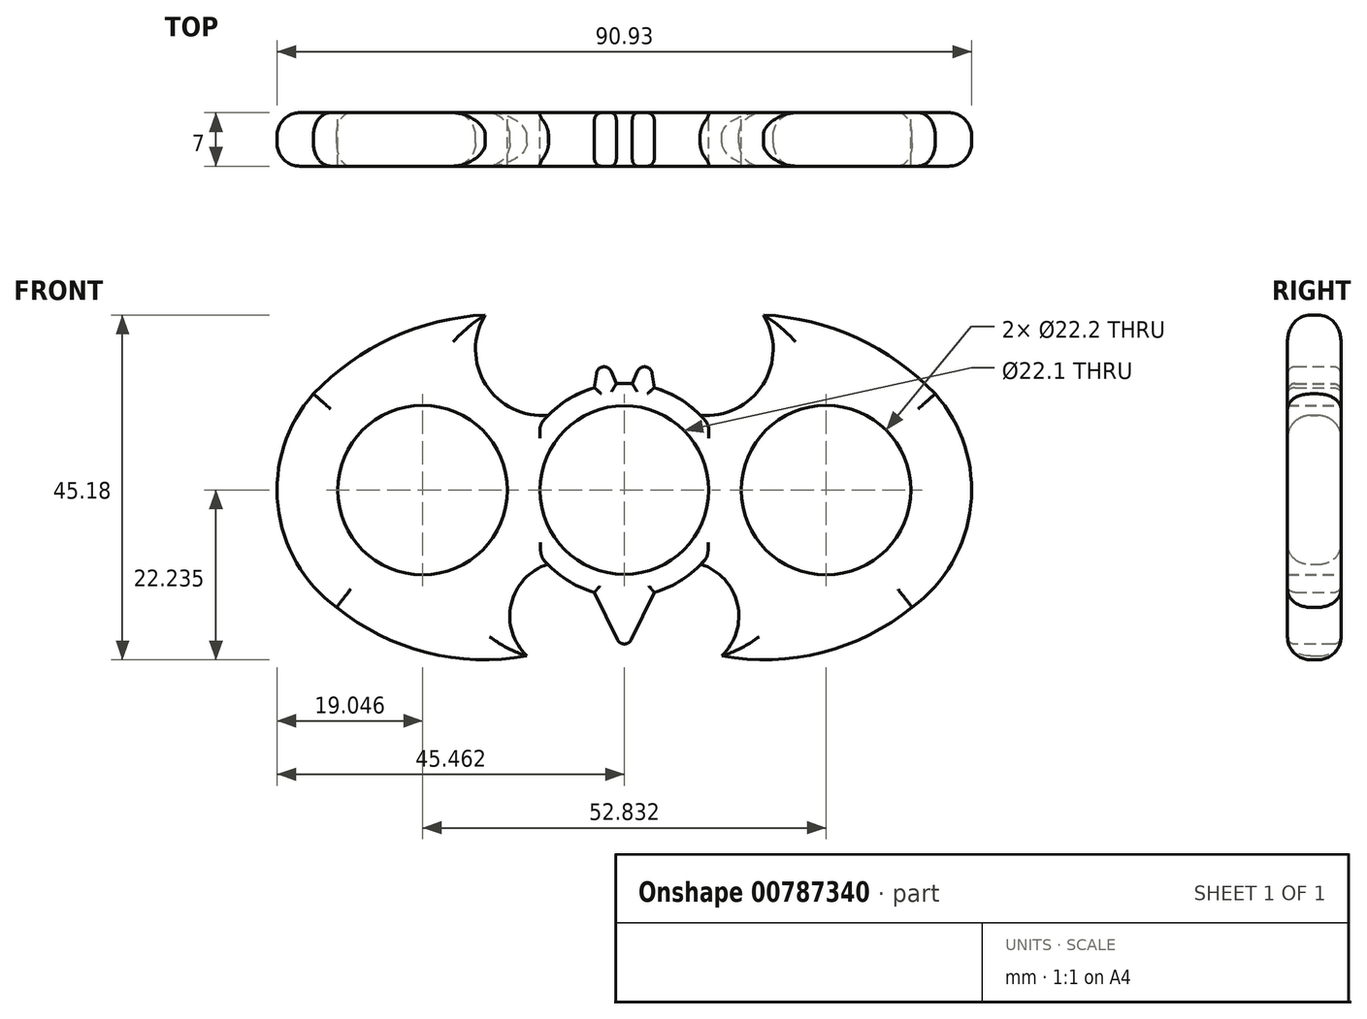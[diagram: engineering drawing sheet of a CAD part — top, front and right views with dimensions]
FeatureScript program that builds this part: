
annotation { "Feature Type Name" : "Feature", "Feature Type Description" : "" }
export const myFeature = defineFeature(function(context is Context, id is Id, definition is map)
    precondition{}
    {
        {
            var Q0;
            Q0=qCreatedBy(makeId("Front.planeOp"),FACE);
            var sketch = newSketch(context, id + "F0", { "sketchPlane" : qUnion([Q0])});
            skCircle(sketch, "E0", {"center": v(17.42, -21.9) * mm, "radius": 11.05 * mm});
            skCircle(sketch, "E1", {"center": v(17.42, -21.9) * mm, "radius": 13.97 * mm});
            skArc(sketch, "E2", {"start": v(55.1, -37.26) * mm, "mid": v(62.78, -23.94) * mm, "end": v(58.12, -9.3) * mm});
            skArc(sketch, "E3", {"start": v(-0.79, 1.05) * mm, "mid": v(-13.03, -1.96) * mm, "end": v(-23.28, -9.3) * mm});
            skArc(sketch, "E4", {"start": v(-0.79, 1.05) * mm, "mid": v(-0.73, -8.08) * mm, "end": v(7.5, -12.07) * mm});
            skArc(sketch, "E5.trimOffspring", {"start": v(-23.28, -9.3) * mm, "mid": v(-27.93, -23.94) * mm, "end": v(-20.26, -37.26) * mm});
            skArc(sketch, "E6.MirrorCS", {"start": v(35.63, 1.05) * mm, "mid": v(35.57, -8.08) * mm, "end": v(27.35, -12.07) * mm});
            skArc(sketch, "E7.MirrorCS", {"start": v(35.63, 1.05) * mm, "mid": v(47.87, -1.96) * mm, "end": v(58.12, -9.3) * mm});
            skArc(sketch, "E8", {"start": v(-20.26, -37.26) * mm, "mid": v(-8.5, -43.17) * mm, "end": v(4.66, -43.63) * mm});
            skArc(sketch, "E9", {"start": v(7.39, -31.62) * mm, "mid": v(2.6, -36.85) * mm, "end": v(4.66, -43.63) * mm});
            skArc(sketch, "E10.MirrorCS", {"start": v(27.45, -31.62) * mm, "mid": v(32.23, -36.85) * mm, "end": v(30.18, -43.63) * mm});
            skArc(sketch, "E11.MirrorCS", {"start": v(55.1, -37.26) * mm, "mid": v(43.34, -43.17) * mm, "end": v(30.18, -43.63) * mm});
            skPoint(sketch, "E12.end.orphan", {"position": v(19.76, -3.07) * mm});
            skPoint(sketch, "E13.orphan", {"position": v(21.34, -8.49) * mm});
            skPoint(sketch, "E14.end.orphan", {"position": v(16.38, -7.96) * mm});
            skPoint(sketch, "E15.end.orphan", {"position": v(15.2, -3.07) * mm});
            skPoint(sketch, "E16.MirrorCS.end.orphan", {"position": v(18.46, -7.96) * mm});
            skPoint(sketch, "E16.MirrorCS.start.orphan", {"position": v(19.65, -3.07) * mm});
            skPoint(sketch, "E17.end.orphan", {"position": v(12.61, -3.54) * mm});
            skPoint(sketch, "E18.MirrorCS.end.orphan", {"position": v(22.23, -3.54) * mm});
            skLineSegment(sketch, "E19", {"start": v(16.38, -7.96) * mm, "end": v(14.32, -3.06) * mm});
            skLineSegment(sketch, "E20", {"start": v(14.32, -3.06) * mm, "end": v(13.5, -8.49) * mm});
            skLineSegment(sketch, "E21.MirrorCS", {"start": v(18.46, -7.96) * mm, "end": v(20.52, -3.06) * mm});
            skLineSegment(sketch, "E22.MirrorCS", {"start": v(20.52, -3.06) * mm, "end": v(21.34, -8.49) * mm});
            skPoint(sketch, "E23.end.orphan", {"position": v(17.42, -43.35) * mm});
            skPoint(sketch, "E23.start.orphan", {"position": v(13.41, -35.28) * mm});
            skPoint(sketch, "E24.MirrorCS.start.orphan", {"position": v(21.43, -35.28) * mm});
            skPoint(sketch, "E25.MirrorCS.end.orphan", {"position": v(13.5, -35.3) * mm});
            skPoint(sketch, "E25.MirrorCS.start.orphan", {"position": v(14.32, -40.73) * mm});
            skLineSegment(sketch, "E26", {"start": v(13.5, -35.3) * mm, "end": v(17.42, -43.35) * mm});
            skLineSegment(sketch, "E27.MirrorCS", {"start": v(21.34, -35.3) * mm, "end": v(17.42, -43.35) * mm});
            skLineSegment(sketch, "E28", {"start": v(-9, -21.9) * mm, "end": v(-13.74, -21.9) * mm});
            skLineSegment(sketch, "E29", {"start": v(43.84, -21.9) * mm, "end": v(48.58, -21.9) * mm});
            skCircle(sketch, "E30", {"center": v(-9, -21.9) * mm, "radius": 11.1 * mm});
            skCircle(sketch, "E31", {"center": v(43.84, -21.9) * mm, "radius": 11.1 * mm});
            skSolve(sketch);
        }
        {
            var Q0;
            Q0=makeQuery(id+"F0.imprint","IMPRINT",FACE,{"disambiguationData":[TD([[makeQuery(id+"F0.imprint","IMPRINT",EDGE,{"derivedFrom":sQuery(id+"F0.wireOp",EDGE,"E3")}),1.0]])]});
            var Q1;
            {var subQ0=sQuery(id+"F0.wireOp",EDGE,"E21.MirrorCS");Q1=makeQuery(id+"F0.imprint","IMPRINT",FACE,{"disambiguationData":[TD([[makeQuery(id+"F0.imprint","IMPRINT",EDGE,{"derivedFrom":subQ0}),-1.0]])]});}
            var Q2;
            {var subQ0=sQuery(id+"F0.wireOp",EDGE,"E19");Q2=makeQuery(id+"F0.imprint","IMPRINT",FACE,{"disambiguationData":[TD([[makeQuery(id+"F0.imprint","IMPRINT",EDGE,{"derivedFrom":subQ0}),1.0]])]});}
            var Q3;
            {var subQ0=sQuery(id+"F0.wireOp",EDGE,"E26");Q3=makeQuery(id+"F0.imprint","IMPRINT",FACE,{"disambiguationData":[TD([[makeQuery(id+"F0.imprint","IMPRINT",EDGE,{"derivedFrom":subQ0}),1.0]])]});}
            var Q4;
            Q4=makeQuery(id+"F0.imprint","IMPRINT",FACE,{"disambiguationData":[TD([[makeQuery(id+"F0.imprint","IMPRINT",EDGE,{"derivedFrom":sQuery(id+"F0.wireOp",EDGE,"E0")}),-1.0]])]});
            var Q5;
            Q5=makeQuery(id+"F0.imprint","IMPRINT",FACE,{"disambiguationData":[TD([[makeQuery(id+"F0.imprint","IMPRINT",EDGE,{"derivedFrom":sQuery(id+"F0.wireOp",EDGE,"E2")}),1.0]])]});
            extrude(context, id + "F1", {"entities" : qUnion([Q0, Q1, Q2, Q3, Q4, Q5]), "depth" : 7 * mm, "offsetDistance" : 25 * mm});
        }
        {
            var Q0;
            Q0=makeQuery(id+"F1.opExtrude","CAP_EDGE",EDGE,{"disambiguationData":[OSD([sQuery(id+"F0.wireOp",EDGE,"E5.trimOffspring")])],"isStart":false});
            var Q1;
            Q1=makeQuery(id+"F1.opExtrude","CAP_EDGE",EDGE,{"disambiguationData":[OSD([sQuery(id+"F0.wireOp",EDGE,"E2")])],"isStart":false});
            var Q2;
            Q2=makeQuery(id+"F1.opExtrude","CAP_EDGE",EDGE,{"disambiguationData":[OSD([sQuery(id+"F0.wireOp",EDGE,"E3")])],"isStart":true});
            var Q3;
            Q3=makeQuery(id+"F1.opExtrude","CAP_EDGE",EDGE,{"disambiguationData":[OSD([sQuery(id+"F0.wireOp",EDGE,"E7.MirrorCS")])],"isStart":true});
            var Q4;
            Q4=makeQuery(id+"F1.opExtrude","CAP_EDGE",EDGE,{"disambiguationData":[OSD([sQuery(id+"F0.wireOp",EDGE,"E6.MirrorCS")])],"isStart":false});
            var Q5;
            Q5=makeQuery(id+"F1.opExtrude","CAP_EDGE",EDGE,{"disambiguationData":[OSD([sQuery(id+"F0.wireOp",EDGE,"E10.MirrorCS")])],"isStart":false});
            var Q6;
            Q6=makeQuery(id+"F1.opExtrude","CAP_EDGE",EDGE,{"disambiguationData":[OSD([sQuery(id+"F0.wireOp",EDGE,"E9")])],"isStart":false});
            var Q7;
            Q7=makeQuery(id+"F1.opExtrude","CAP_EDGE",EDGE,{"disambiguationData":[OSD([sQuery(id+"F0.wireOp",EDGE,"E4")])],"isStart":false});
            var Q8;
            Q8=makeQuery(id+"F1.opExtrude","CAP_EDGE",EDGE,{"disambiguationData":[OSD([sQuery(id+"F0.wireOp",EDGE,"E4")])],"isStart":true});
            var Q9;
            Q9=makeQuery(id+"F1.opExtrude","CAP_EDGE",EDGE,{"disambiguationData":[OSD([sQuery(id+"F0.wireOp",EDGE,"E9")])],"isStart":true});
            var Q10;
            Q10=makeQuery(id+"F1.opExtrude","CAP_EDGE",EDGE,{"disambiguationData":[OSD([sQuery(id+"F0.wireOp",EDGE,"E6.MirrorCS")])],"isStart":true});
            var Q11;
            Q11=makeQuery(id+"F1.opExtrude","CAP_EDGE",EDGE,{"disambiguationData":[OSD([sQuery(id+"F0.wireOp",EDGE,"E10.MirrorCS")])],"isStart":true});
            var Q12;
            Q12=makeQuery(id+"F1.opExtrude","CAP_EDGE",EDGE,{"disambiguationData":[OSD([sQuery(id+"F0.wireOp",EDGE,"E11.MirrorCS")])],"isStart":true});
            var Q13;
            Q13=makeQuery(id+"F1.opExtrude","CAP_EDGE",EDGE,{"disambiguationData":[OSD([sQuery(id+"F0.wireOp",EDGE,"E2")])],"isStart":true});
            var Q14;
            Q14=makeQuery(id+"F1.opExtrude","CAP_EDGE",EDGE,{"disambiguationData":[OSD([sQuery(id+"F0.wireOp",EDGE,"E5.trimOffspring")])],"isStart":true});
            fillet(context, id + "F2", {"entities" : qUnion([Q0, Q1, Q2, Q3, Q4, Q5, Q6, Q7, Q8, Q9, Q10, Q11, Q12, Q13, Q14]), "radius" : 3 * mm, "tangentPropagation" : true, "allowEdgeOverflow" : false});
        }
        {
            var Q0;
            {var subQ0=sQuery(id+"F0.wireOp",EDGE,"E1");Q0=makeQuery(id+"F1.opExtrude","CAP_EDGE",EDGE,{"disambiguationData":[OSD([subQ0]),TDD([makeQuery(id+"F0.imprint","IMPRINT",EDGE,{"disambiguationData":[TD([[makeQuery(id+"F0.imprint","INTERSECT",VERTEX,{"derivedFrom":[subQ0,sQuery(id+"F0.wireOp",EDGE,"E10.MirrorCS")]}),1.0]])],"derivedFrom":subQ0})])],"isStart":true});}
            var Q1;
            Q1=makeQuery(id+"F1.opExtrude","CAP_EDGE",EDGE,{"disambiguationData":[OSD([sQuery(id+"F0.wireOp",EDGE,"E21.MirrorCS")])],"isStart":true});
            var Q2;
            Q2=makeQuery(id+"F1.opExtrude","CAP_EDGE",EDGE,{"disambiguationData":[OSD([sQuery(id+"F0.wireOp",EDGE,"E22.MirrorCS")])],"isStart":true});
            var Q3;
            Q3=makeQuery(id+"F1.opExtrude","CAP_EDGE",EDGE,{"disambiguationData":[OSD([sQuery(id+"F0.wireOp",EDGE,"E19")])],"isStart":true});
            var Q4;
            Q4=makeQuery(id+"F1.opExtrude","CAP_EDGE",EDGE,{"disambiguationData":[OSD([sQuery(id+"F0.wireOp",EDGE,"E20")])],"isStart":true});
            var Q5;
            {var subQ0=sQuery(id+"F0.wireOp",EDGE,"E1");Q5=makeQuery(id+"F1.opExtrude","CAP_EDGE",EDGE,{"disambiguationData":[OSD([subQ0]),TDD([makeQuery(id+"F0.imprint","IMPRINT",EDGE,{"disambiguationData":[TD([[makeQuery(id+"F0.imprint","INTERSECT",VERTEX,{"derivedFrom":[subQ0,sQuery(id+"F0.wireOp",EDGE,"E6.MirrorCS")]}),-1.0]])],"derivedFrom":subQ0})])],"isStart":true});}
            var Q6;
            {var subQ0=sQuery(id+"F0.wireOp",EDGE,"E1");Q6=makeQuery(id+"F1.opExtrude","CAP_EDGE",EDGE,{"disambiguationData":[OSD([subQ0]),TDD([makeQuery(id+"F0.imprint","IMPRINT",EDGE,{"disambiguationData":[TD([[makeQuery(id+"F0.imprint","INTERSECT",VERTEX,{"derivedFrom":[subQ0,sQuery(id+"F0.wireOp",EDGE,"E19")]}),1.0]])],"derivedFrom":subQ0})])],"isStart":true});}
            var Q7;
            {var subQ0=sQuery(id+"F0.wireOp",EDGE,"E1");Q7=makeQuery(id+"F1.opExtrude","CAP_EDGE",EDGE,{"disambiguationData":[OSD([subQ0]),TDD([makeQuery(id+"F0.imprint","IMPRINT",EDGE,{"disambiguationData":[TD([[makeQuery(id+"F0.imprint","INTERSECT",VERTEX,{"derivedFrom":[subQ0,sQuery(id+"F0.wireOp",EDGE,"E4")]}),1.0]])],"derivedFrom":subQ0})])],"isStart":true});}
            var Q8;
            {var subQ0=sQuery(id+"F0.wireOp",EDGE,"E1");Q8=makeQuery(id+"F1.opExtrude","CAP_EDGE",EDGE,{"disambiguationData":[OSD([subQ0]),TDD([makeQuery(id+"F0.imprint","IMPRINT",EDGE,{"disambiguationData":[TD([[makeQuery(id+"F0.imprint","INTERSECT",VERTEX,{"derivedFrom":[subQ0,sQuery(id+"F0.wireOp",EDGE,"E6.MirrorCS")]}),-1.0]])],"derivedFrom":subQ0})])],"isStart":false});}
            var Q9;
            Q9=makeQuery(id+"F1.opExtrude","CAP_EDGE",EDGE,{"disambiguationData":[OSD([sQuery(id+"F0.wireOp",EDGE,"E22.MirrorCS")])],"isStart":false});
            var Q10;
            Q10=makeQuery(id+"F1.opExtrude","CAP_EDGE",EDGE,{"disambiguationData":[OSD([sQuery(id+"F0.wireOp",EDGE,"E21.MirrorCS")])],"isStart":false});
            var Q11;
            {var subQ0=sQuery(id+"F0.wireOp",EDGE,"E1");Q11=makeQuery(id+"F1.opExtrude","CAP_EDGE",EDGE,{"disambiguationData":[OSD([subQ0]),TDD([makeQuery(id+"F0.imprint","IMPRINT",EDGE,{"disambiguationData":[TD([[makeQuery(id+"F0.imprint","INTERSECT",VERTEX,{"derivedFrom":[subQ0,sQuery(id+"F0.wireOp",EDGE,"E19")]}),1.0]])],"derivedFrom":subQ0})])],"isStart":false});}
            var Q12;
            Q12=makeQuery(id+"F1.opExtrude","CAP_EDGE",EDGE,{"disambiguationData":[OSD([sQuery(id+"F0.wireOp",EDGE,"E19")])],"isStart":false});
            var Q13;
            Q13=makeQuery(id+"F1.opExtrude","CAP_EDGE",EDGE,{"disambiguationData":[OSD([sQuery(id+"F0.wireOp",EDGE,"E20")])],"isStart":false});
            var Q14;
            {var subQ0=sQuery(id+"F0.wireOp",EDGE,"E1");Q14=makeQuery(id+"F1.opExtrude","CAP_EDGE",EDGE,{"disambiguationData":[OSD([subQ0]),TDD([makeQuery(id+"F0.imprint","IMPRINT",EDGE,{"disambiguationData":[TD([[makeQuery(id+"F0.imprint","INTERSECT",VERTEX,{"derivedFrom":[subQ0,sQuery(id+"F0.wireOp",EDGE,"E4")]}),1.0]])],"derivedFrom":subQ0})])],"isStart":false});}
            var Q15;
            {var subQ0=sQuery(id+"F0.wireOp",EDGE,"E1");Q15=makeQuery(id+"F1.opExtrude","CAP_EDGE",EDGE,{"disambiguationData":[OSD([subQ0]),TDD([makeQuery(id+"F0.imprint","IMPRINT",EDGE,{"disambiguationData":[TD([[makeQuery(id+"F0.imprint","INTERSECT",VERTEX,{"derivedFrom":[subQ0,sQuery(id+"F0.wireOp",EDGE,"E10.MirrorCS")]}),1.0]])],"derivedFrom":subQ0})])],"isStart":false});}
            var Q16;
            {var subQ0=sQuery(id+"F0.wireOp",EDGE,"E1");Q16=makeQuery(id+"F1.opExtrude","CAP_EDGE",EDGE,{"disambiguationData":[OSD([subQ0]),TDD([makeQuery(id+"F0.imprint","IMPRINT",EDGE,{"disambiguationData":[TD([[makeQuery(id+"F0.imprint","INTERSECT",VERTEX,{"derivedFrom":[subQ0,sQuery(id+"F0.wireOp",EDGE,"E9")]}),-1.0]])],"derivedFrom":subQ0})])],"isStart":false});}
            var Q17;
            Q17=makeQuery(id+"F1.opExtrude","CAP_EDGE",EDGE,{"disambiguationData":[OSD([sQuery(id+"F0.wireOp",EDGE,"E26")])],"isStart":false});
            var Q18;
            Q18=makeQuery(id+"F1.opExtrude","CAP_EDGE",EDGE,{"disambiguationData":[OSD([sQuery(id+"F0.wireOp",EDGE,"E27.MirrorCS")])],"isStart":false});
            var Q19;
            Q19=makeQuery(id+"F1.opExtrude","CAP_EDGE",EDGE,{"disambiguationData":[OSD([sQuery(id+"F0.wireOp",EDGE,"E27.MirrorCS")])],"isStart":true});
            var Q20;
            {var subQ0=sQuery(id+"F0.wireOp",EDGE,"E1");Q20=makeQuery(id+"F1.opExtrude","CAP_EDGE",EDGE,{"disambiguationData":[OSD([subQ0]),TDD([makeQuery(id+"F0.imprint","IMPRINT",EDGE,{"disambiguationData":[TD([[makeQuery(id+"F0.imprint","INTERSECT",VERTEX,{"derivedFrom":[subQ0,sQuery(id+"F0.wireOp",EDGE,"E9")]}),-1.0]])],"derivedFrom":subQ0})])],"isStart":true});}
            var Q21;
            Q21=makeQuery(id+"F1.opExtrude","CAP_EDGE",EDGE,{"disambiguationData":[OSD([sQuery(id+"F0.wireOp",EDGE,"E26")])],"isStart":true});
            var Q22;
            Q22=makeQuery(id+"F1.opExtrude","SWEPT_EDGE",EDGE,{"disambiguationData":[OSD([sQuery(id+"F0.wireOp",EDGE,"E26"),sQuery(id+"F0.wireOp",EDGE,"E27.MirrorCS")])]});
            var Q23;
            Q23=makeQuery(id+"F1.opExtrude","SWEPT_EDGE",EDGE,{"disambiguationData":[OSD([sQuery(id+"F0.wireOp",EDGE,"E19"),sQuery(id+"F0.wireOp",EDGE,"E20")])]});
            var Q24;
            Q24=makeQuery(id+"F1.opExtrude","SWEPT_EDGE",EDGE,{"disambiguationData":[OSD([sQuery(id+"F0.wireOp",EDGE,"E21.MirrorCS"),sQuery(id+"F0.wireOp",EDGE,"E22.MirrorCS")])]});
            fillet(context, id + "F3", {"entities" : qUnion([Q0, Q1, Q2, Q3, Q4, Q5, Q6, Q7, Q8, Q9, Q10, Q11, Q12, Q13, Q14, Q15, Q16, Q17, Q18, Q19, Q20, Q21, Q22, Q23, Q24]), "radius" : 1 * mm, "tangentPropagation" : true, "allowEdgeOverflow" : false});
        }
    });
